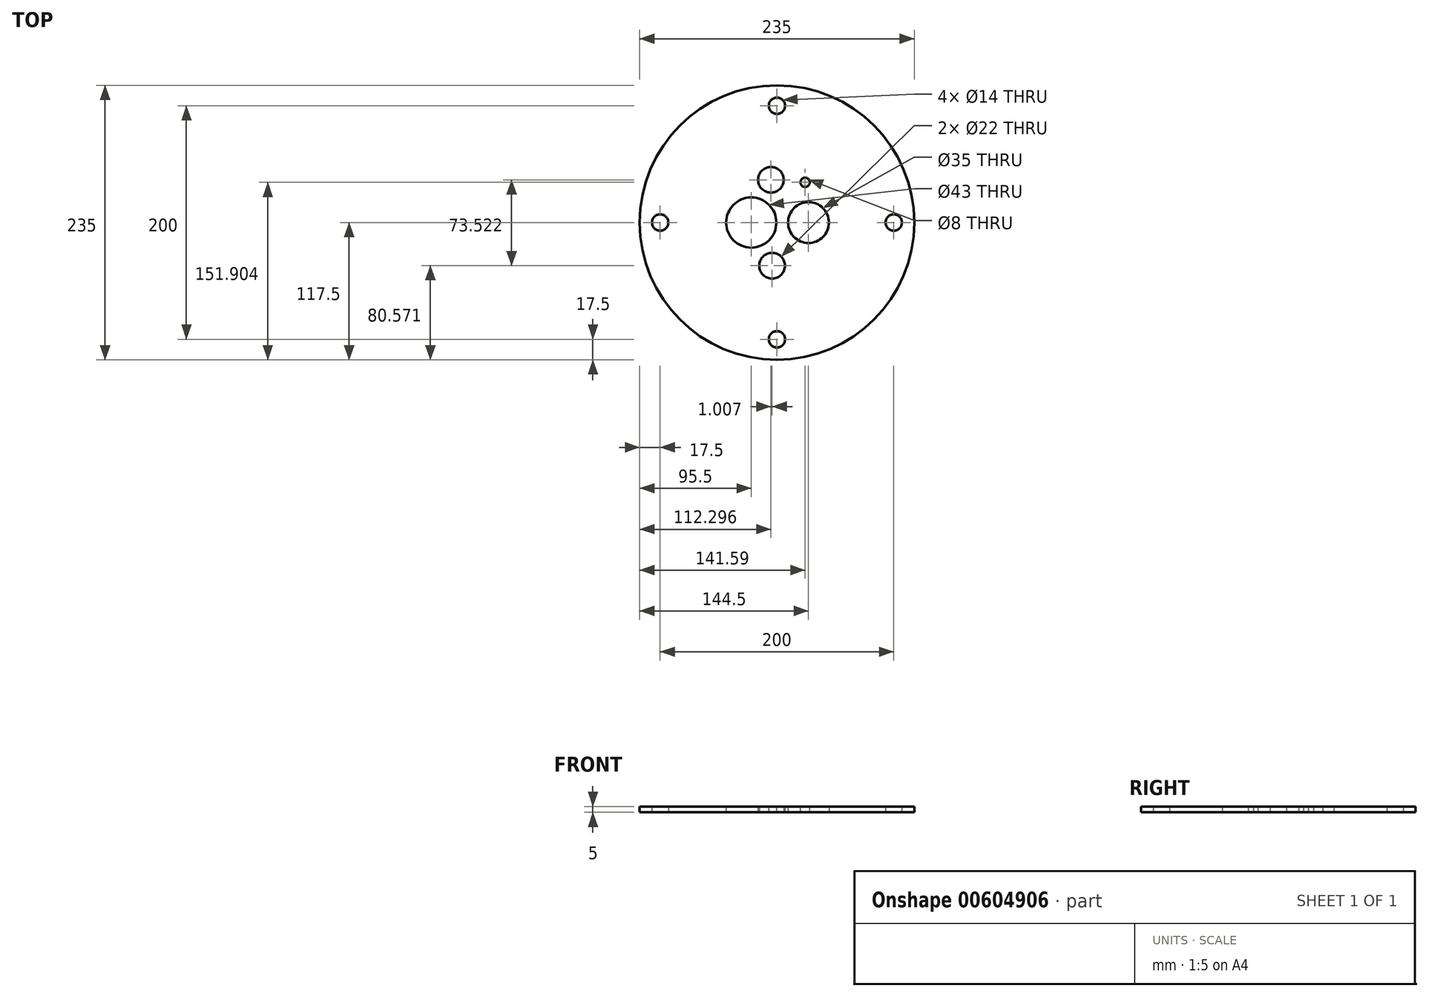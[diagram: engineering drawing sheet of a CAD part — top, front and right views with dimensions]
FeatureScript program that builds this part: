
annotation { "Feature Type Name" : "Feature", "Feature Type Description" : "" }
export const myFeature = defineFeature(function(context is Context, id is Id, definition is map)
    precondition{}
    {
        {
            var Q0;
            Q0=qCreatedBy(makeId("Top.planeOp"),FACE);
            var sketch = newSketch(context, id + "F0", { "sketchPlane" : qUnion([Q0])});
            skLineSegment(sketch, "E0", {"start": v(-63.5, 0) * mm, "end": v(117.5, 0) * mm, "construction": true});
            skCircle(sketch, "E1", {"center": v(0, 0) * mm, "radius": 117.5 * mm});
            skCircle(sketch, "E2", {"center": v(0, 0) * mm, "radius": 55 * mm, "construction": true});
            skLineSegment(sketch, "E3", {"start": v(0, 0) * mm, "end": v(0, -73.71) * mm, "construction": true});
            skCircle(sketch, "E4", {"center": v(-4.2, -36.93) * mm, "radius": 11 * mm});
            skCircle(sketch, "E5", {"center": v(0, 0) * mm, "radius": 85 * mm, "construction": true});
            skLineSegment(sketch, "E6", {"start": v(0, 0) * mm, "end": v(0, 73.19) * mm, "construction": true});
            skCircle(sketch, "E7", {"center": v(-5.2, 36.6) * mm, "radius": 11 * mm});
            skCircle(sketch, "E8", {"center": v(27, 0) * mm, "radius": 17.5 * mm});
            skCircle(sketch, "E9", {"center": v(-22, 0) * mm, "radius": 21.5 * mm});
            skPoint(sketch, "E10", {"position": v(0, 36.6) * mm});
            skCircle(sketch, "E11", {"center": v(-4.2, -36.93) * mm, "radius": 16 * mm, "construction": true});
            skCircle(sketch, "E12", {"center": v(-5.2, 36.6) * mm, "radius": 16 * mm, "construction": true});
            skSolve(sketch);
        }
        {
            var Q0;
            Q0 = qSketchRegion(id + "F0", true);
            extrude(context, id + "F1", {"entities" : qUnion([Q0]), "depth" : 5 * mm, "offsetDistance" : 25 * mm});
        }
        {
            var Q0;
            Q0=makeQuery(id+"F1.opExtrude","CAP_FACE",FACE,{"disambiguationData":[OSD([sQuery(id+"F0.wireOp",EDGE,"E1")])],"isStart":true});
            var sketch = newSketch(context, id + "F2", { "sketchPlane" : qUnion([Q0])});
            skCircle(sketch, "E13", {"center": v(0, 0) * mm, "radius": 100 * mm, "construction": true});
            skLineSegment(sketch, "E14", {"start": v(-100, 0) * mm, "end": v(100, 0) * mm, "construction": true});
            skLineSegment(sketch, "E15", {"start": v(0, 100) * mm, "end": v(0, -100) * mm, "construction": true});
            skCircle(sketch, "E16", {"center": v(-100, 0) * mm, "radius": 7 * mm});
            skCircle(sketch, "E17", {"center": v(0, 100) * mm, "radius": 7 * mm});
            skCircle(sketch, "E18", {"center": v(100, 0) * mm, "radius": 7 * mm});
            skCircle(sketch, "E19", {"center": v(0, -100) * mm, "radius": 7 * mm});
            skSolve(sketch);
        }
        {
            var Q0;
            Q0 = qSketchRegion(id + "F2", true);
            extrude(context, id + "F3", {"entities" : qUnion([Q0]), "operationType" : NewBodyOperationType.REMOVE, "endBound" : BoundingType.THROUGH_ALL, "oppositeDirection" : true, "depth" : 25 * mm, "offsetDistance" : 25 * mm});
        }
        {
            var Q0;
            Q0=makeQuery(id+"F1.opExtrude","CAP_FACE",FACE,{"disambiguationData":[OSD([sQuery(id+"F0.wireOp",EDGE,"E1"),sQuery(id+"F0.wireOp",EDGE,"E4"),sQuery(id+"F0.wireOp",EDGE,"E7"),sQuery(id+"F0.wireOp",EDGE,"E8"),sQuery(id+"F0.wireOp",EDGE,"E9")])],"isStart":false});
            var sketch = newSketch(context, id + "F4", { "sketchPlane" : qUnion([Q0])});
            skLineSegment(sketch, "E20", {"start": v(0, 0) * mm, "end": v(0, 54.39) * mm, "construction": true});
            skCircle(sketch, "E21.MirrorC", {"center": v(24.1, 34.4) * mm, "radius": 4 * mm});
            skLineSegment(sketch, "E22", {"start": v(0, 0) * mm, "end": v(24.1, 34.4) * mm, "construction": true});
            skSolve(sketch);
        }
        {
            var Q0;
            Q0 = qSketchRegion(id + "F4", true);
            extrude(context, id + "F5", {"entities" : qUnion([Q0]), "operationType" : NewBodyOperationType.REMOVE, "endBound" : BoundingType.THROUGH_ALL, "oppositeDirection" : true, "depth" : 25 * mm, "offsetDistance" : 25 * mm});
        }
    });
